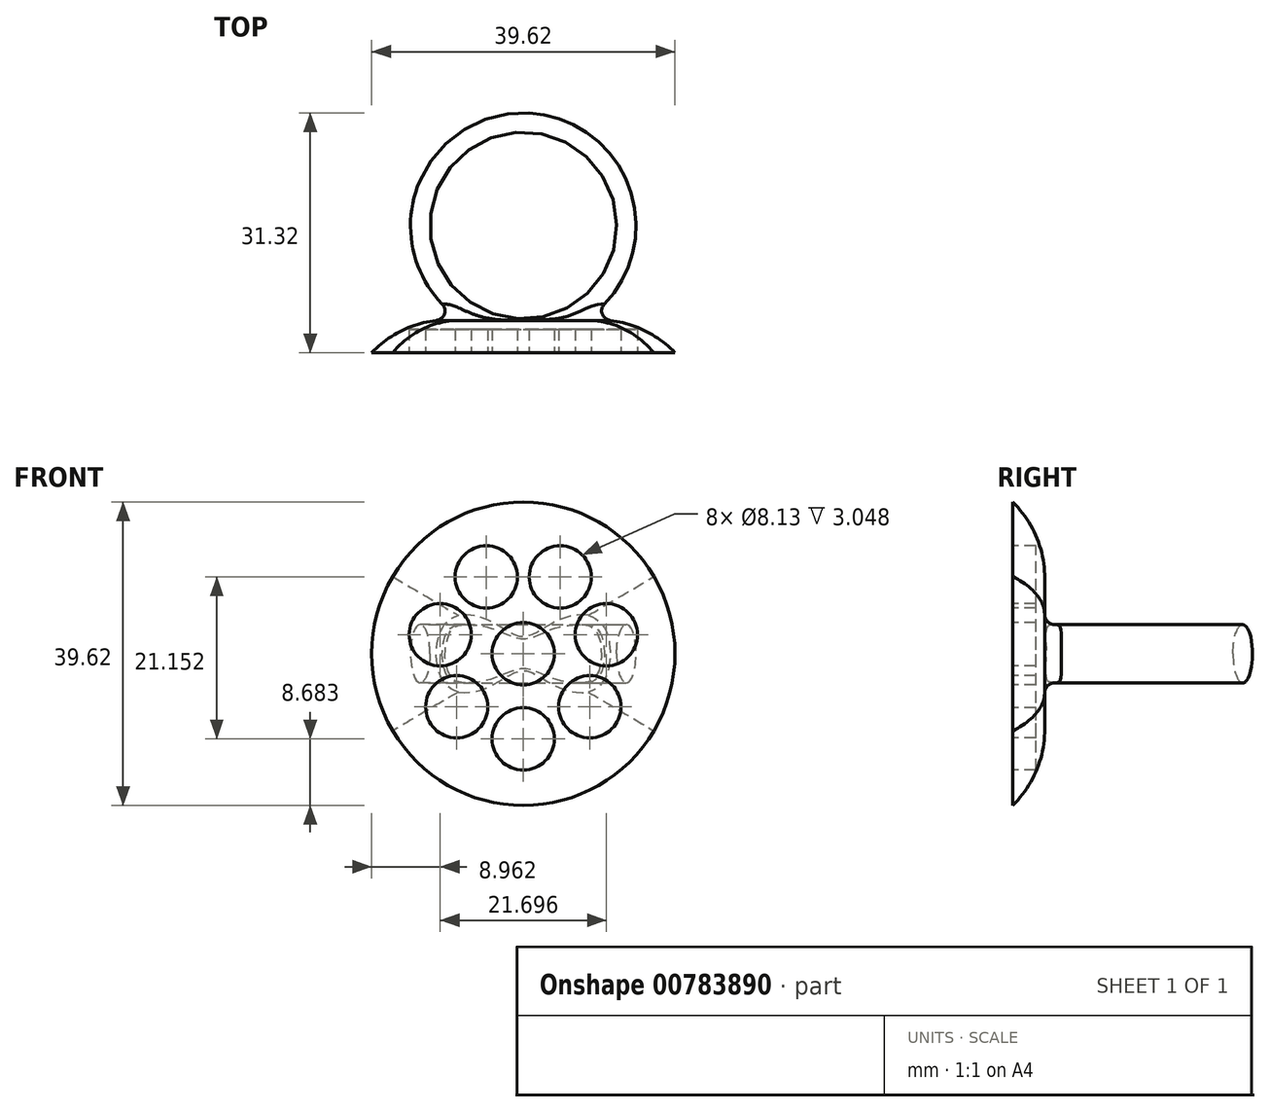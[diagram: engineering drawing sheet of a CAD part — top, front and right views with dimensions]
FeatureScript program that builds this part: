
annotation { "Feature Type Name" : "Feature", "Feature Type Description" : "" }
export const myFeature = defineFeature(function(context is Context, id is Id, definition is map)
    precondition{}
    {
        {
            var Q0;
            Q0=qCreatedBy(makeId("Top.planeOp"),FACE);
            var sketch = newSketch(context, id + "F0", { "sketchPlane" : qUnion([Q0])});
            skCircle(sketch, "E0", {"center": v(0, 0) * mm, "radius": 18.4 * mm});
            skLineSegment(sketch, "E1", {"start": v(0, 0) * mm, "end": v(0, -18.4) * mm});
            skLineSegment(sketch, "E2", {"start": v(0, -18.4) * mm, "end": v(0, 18.4) * mm});
            skPoint(sketch, "E3", {"position": v(0, 18.4) * mm});
            skPoint(sketch, "E4", {"position": v(0, -18.4) * mm});
            skSolve(sketch);
        }
        {
            var Q0;
            Q0=qCreatedBy(makeId("Right.planeOp"),FACE);
            var sketch = newSketch(context, id + "F1", { "sketchPlane" : qUnion([Q0])});
            skEllipse(sketch, "E5", {"center": v(13.46, 0) * mm, "majorRadius": 3.81 * mm, "minorRadius": 1.27 * mm, "majorAxis": v(0, 1)});
            skLineSegment(sketch, "E6", {"start": v(0, 0) * mm, "end": v(0, 21.06) * mm});
            skLineSegment(sketch, "E7", {"start": v(12.2, 0) * mm, "end": v(12.2, -14.12) * mm, "construction": true});
            skLineSegment(sketch, "E8", {"start": v(12.2, -14.12) * mm, "end": v(0, -14.12) * mm, "construction": true});
            skLineSegment(sketch, "E9", {"start": v(0, -14.12) * mm, "end": v(0, 0) * mm, "construction": true});
            skSolve(sketch);
        }
        {
            var Q0;
            Q0 = qSketchRegion(id + "F1", true);
            var Q1;
            Q1=sQuery(id+"F1.wireOp",EDGE,"E6");
            revolve(context, id + "F2", {"surfaceOperationType" : NewSurfaceOperationType.NEW, "entities" : qUnion([Q0]), "axis" : qUnion([Q1]), "revolveType" : RevolveType.FULL});
        }
        {
            var Q0;
            Q0=qCreatedBy(makeId("Top.planeOp"),FACE);
            var sketch = newSketch(context, id + "F3", { "sketchPlane" : qUnion([Q0])});
            skLineSegment(sketch, "E10", {"start": v(0, -12.4) * mm, "end": v(19.81, -12.4) * mm});
            skLineSegment(sketch, "E11", {"start": v(19.81, -12.4) * mm, "end": v(19.81, -16.59) * mm});
            skLineSegment(sketch, "E12", {"start": v(19.81, -16.59) * mm, "end": v(0, -16.59) * mm});
            skLineSegment(sketch, "E13", {"start": v(0, -12.4) * mm, "end": v(0, -16.59) * mm});
            skSolve(sketch);
        }
        {
            var Q0;
            Q0=makeQuery(id+"F3.imprint","IMPRINT",FACE,{"disambiguationData":[TD([[makeQuery(id+"F3.imprint","IMPRINT",EDGE,{"derivedFrom":sQuery(id+"F3.wireOp",EDGE,"E10")}),-1.0]])]});
            var Q1;
            Q1=sQuery(id+"F3.wireOp",EDGE,"E12");
            var Q2;
            Q2=sQuery(id+"F3.wireOp",EDGE,"E11");
            var Q3;
            Q3=sQuery(id+"F3.wireOp",EDGE,"E10");
            var Q4;
            Q4=sQuery(id+"F3.wireOp",EDGE,"E13");
            var Q5;
            Q5=sQuery(id+"F0.wireOp",EDGE,"E2");
            revolve(context, id + "F4", {"operationType" : NewBodyOperationType.ADD, "surfaceOperationType" : NewSurfaceOperationType.NEW, "entities" : qUnion([Q0]), "surfaceEntities" : qUnion([Q1, Q2, Q3, Q4]), "axis" : qUnion([Q5]), "revolveType" : RevolveType.FULL});
        }
        {
            var Q0;
            Q0=makeQuery(id+"F4.boolean.opBoolean","INTERSECT",EDGE,{"derivedFrom":[makeQuery(id+"F2.opRevolve","SWEPT_FACE",FACE,{"disambiguationData":[OSD([sQuery(id+"F1.wireOp",EDGE,"E5")])]}),makeQuery(id+"F4.opRevolve","SWEPT_FACE",FACE,{"disambiguationData":[OSD([sQuery(id+"F3.wireOp",EDGE,"E10")])]})]});
            fillet(context, id + "F5", {"entities" : qUnion([Q0]), "radius" : 1.27 * mm, "tangentPropagation" : true, "allowEdgeOverflow" : false});
        }
        {
            var Q0;
            Q0=makeQuery(id+"F4.opRevolve","SWEPT_EDGE",EDGE,{"disambiguationData":[OSD([sQuery(id+"F3.wireOp",EDGE,"E10"),sQuery(id+"F3.wireOp",EDGE,"E11")])]});
            fillet(context, id + "F6", {"entities" : qUnion([Q0]), "radius" : 13.97 * mm, "tangentPropagation" : true, "allowEdgeOverflow" : false});
        }
        {
            var Q0;
            Q0=makeQuery(id+"F4.opRevolve","SWEPT_FACE",FACE,{"disambiguationData":[OSD([sQuery(id+"F3.wireOp",EDGE,"E12")])]});
            var sketch = newSketch(context, id + "F7", { "sketchPlane" : qUnion([Q0])});
            skCircle(sketch, "E14", {"center": v(0, 0) * mm, "radius": 4.06 * mm});
            skCircle(sketch, "E15", {"center": v(0, -11.13) * mm, "radius": 4.06 * mm});
            skCircle(sketch, "E16.1.0", {"center": v(8.7, -6.94) * mm, "radius": 4.06 * mm});
            skCircle(sketch, "E16.2.0", {"center": v(10.85, 2.48) * mm, "radius": 4.06 * mm});
            skCircle(sketch, "E16.3.0", {"center": v(4.83, 10.02) * mm, "radius": 4.06 * mm});
            skCircle(sketch, "E16.4.0", {"center": v(-4.83, 10.02) * mm, "radius": 4.06 * mm});
            skCircle(sketch, "E16.5.0", {"center": v(-10.85, 2.48) * mm, "radius": 4.06 * mm});
            skCircle(sketch, "E16.6.0", {"center": v(-8.7, -6.94) * mm, "radius": 4.06 * mm});
            skSolve(sketch);
        }
        {
            var Q0;
            Q0=makeQuery(id+"F7.imprint","IMPRINT",FACE,{"disambiguationData":[TD([[makeQuery(id+"F7.imprint","IMPRINT",EDGE,{"derivedFrom":sQuery(id+"F7.wireOp",EDGE,"E15")}),1.0]])]});
            var Q1;
            Q1=makeQuery(id+"F7.imprint","IMPRINT",FACE,{"disambiguationData":[TD([[makeQuery(id+"F7.imprint","IMPRINT",EDGE,{"derivedFrom":sQuery(id+"F7.wireOp",EDGE,"E16.6.0")}),1.0]])]});
            var Q2;
            Q2=makeQuery(id+"F7.imprint","IMPRINT",FACE,{"disambiguationData":[TD([[makeQuery(id+"F7.imprint","IMPRINT",EDGE,{"derivedFrom":sQuery(id+"F7.wireOp",EDGE,"E16.1.0")}),1.0]])]});
            var Q3;
            Q3=makeQuery(id+"F7.imprint","IMPRINT",FACE,{"disambiguationData":[TD([[makeQuery(id+"F7.imprint","IMPRINT",EDGE,{"derivedFrom":sQuery(id+"F7.wireOp",EDGE,"E16.2.0")}),1.0]])]});
            var Q4;
            Q4=makeQuery(id+"F7.imprint","IMPRINT",FACE,{"disambiguationData":[TD([[makeQuery(id+"F7.imprint","IMPRINT",EDGE,{"derivedFrom":sQuery(id+"F7.wireOp",EDGE,"E14")}),1.0]])]});
            var Q5;
            Q5=makeQuery(id+"F7.imprint","IMPRINT",FACE,{"disambiguationData":[TD([[makeQuery(id+"F7.imprint","IMPRINT",EDGE,{"derivedFrom":sQuery(id+"F7.wireOp",EDGE,"E16.5.0")}),1.0]])]});
            var Q6;
            Q6=makeQuery(id+"F7.imprint","IMPRINT",FACE,{"disambiguationData":[TD([[makeQuery(id+"F7.imprint","IMPRINT",EDGE,{"derivedFrom":sQuery(id+"F7.wireOp",EDGE,"E16.4.0")}),1.0]])]});
            var Q7;
            Q7=makeQuery(id+"F7.imprint","IMPRINT",FACE,{"disambiguationData":[TD([[makeQuery(id+"F7.imprint","IMPRINT",EDGE,{"derivedFrom":sQuery(id+"F7.wireOp",EDGE,"E16.3.0")}),1.0]])]});
            var Q8;
            Q8=sQuery(id+"F7.wireOp",EDGE,"E15");
            var Q9;
            Q9=sQuery(id+"F7.wireOp",EDGE,"E16.6.0");
            var Q10;
            Q10=sQuery(id+"F7.wireOp",EDGE,"E16.1.0");
            var Q11;
            Q11=sQuery(id+"F7.wireOp",EDGE,"E14");
            var Q12;
            Q12=sQuery(id+"F7.wireOp",EDGE,"E16.5.0");
            var Q13;
            Q13=sQuery(id+"F7.wireOp",EDGE,"E16.4.0");
            var Q14;
            Q14=sQuery(id+"F7.wireOp",EDGE,"E16.3.0");
            var Q15;
            Q15=sQuery(id+"F7.wireOp",EDGE,"E16.2.0");
            extrude(context, id + "F8", {"entities" : qUnion([Q0, Q1, Q2, Q3, Q4, Q5, Q6, Q7]), "operationType" : NewBodyOperationType.REMOVE, "surfaceEntities" : qUnion([Q8, Q9, Q10, Q11, Q12, Q13, Q14, Q15]), "oppositeDirection" : true, "depth" : 3.05 * mm, "offsetDistance" : 25.4 * mm});
        }
    });
